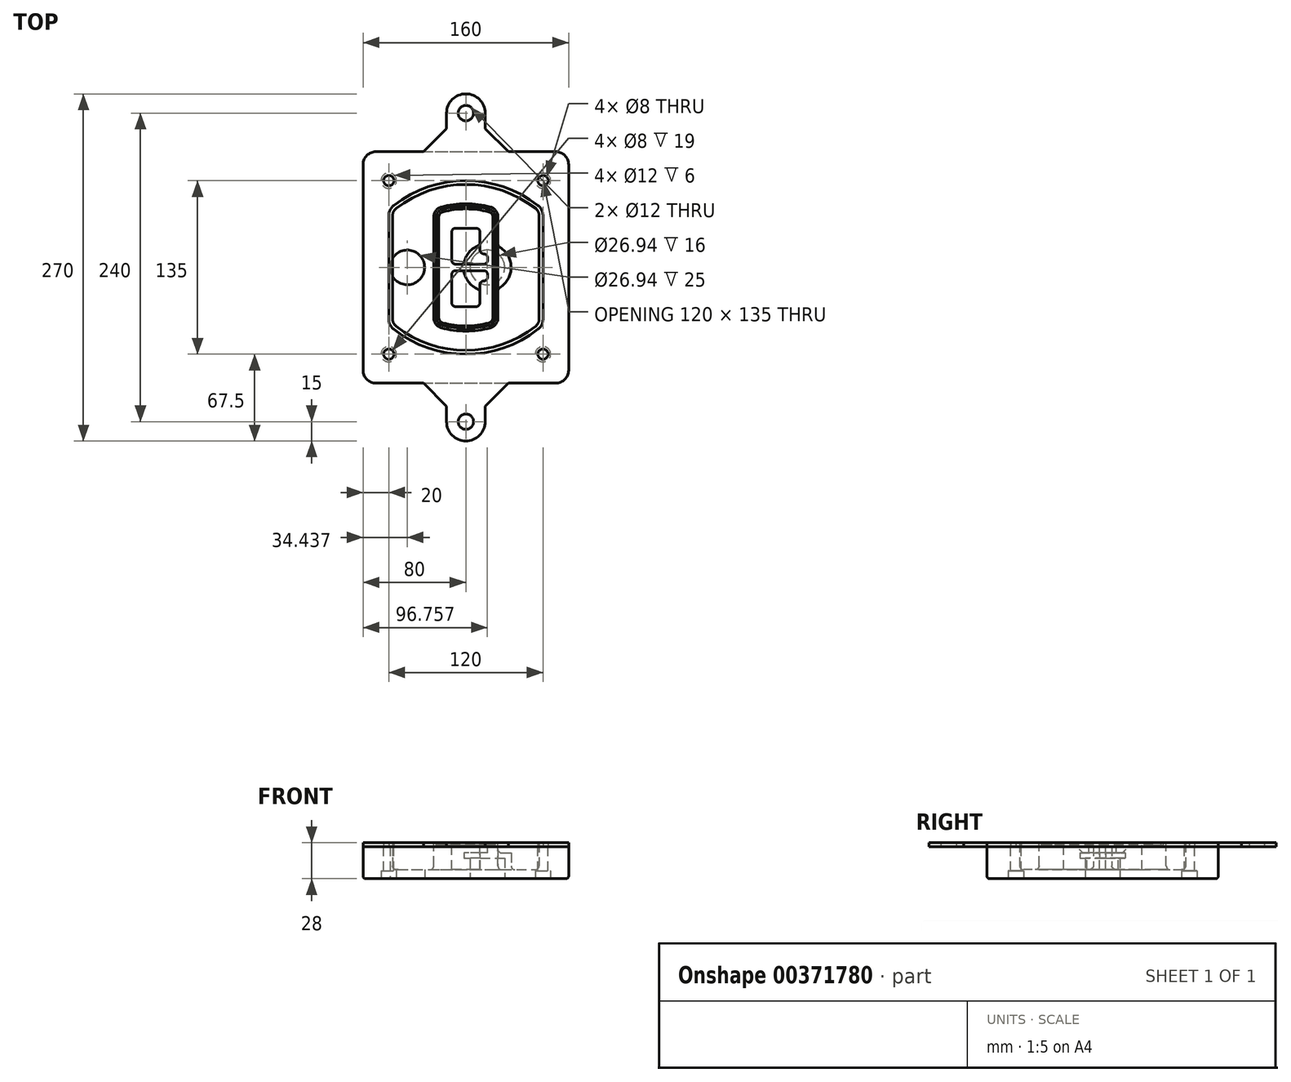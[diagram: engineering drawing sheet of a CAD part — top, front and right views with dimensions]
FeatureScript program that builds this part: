
annotation { "Feature Type Name" : "Feature", "Feature Type Description" : "" }
export const myFeature = defineFeature(function(context is Context, id is Id, definition is map)
    precondition{}
    {
        {
            var Q0;
            Q0=qCreatedBy(makeId("Top.planeOp"),FACE);
            var sketch = newSketch(context, id + "F0", { "sketchPlane" : qUnion([Q0])});
            skPoint(sketch, "E0.rect.middle", {"position": v(0, 0) * mm});
            skLineSegment(sketch, "E1.bottom", {"start": v(-70, -90) * mm, "end": v(70, -90) * mm});
            skLineSegment(sketch, "E1.top", {"start": v(-70, 90) * mm, "end": v(70, 90) * mm});
            skLineSegment(sketch, "E1.left", {"start": v(-80, -80) * mm, "end": v(-80, 80) * mm});
            skLineSegment(sketch, "E1.right", {"start": v(80, -80) * mm, "end": v(80, 80) * mm});
            skLineSegment(sketch, "E2", {"start": v(-80, 90) * mm, "end": v(80, -90) * mm, "construction": true});
            skLineSegment(sketch, "E3", {"start": v(80, 90) * mm, "end": v(-80, -90) * mm, "construction": true});
            skCircle(sketch, "E4", {"center": v(-60, 67.5) * mm, "radius": 4 * mm});
            skCircle(sketch, "E5", {"center": v(60, 67.5) * mm, "radius": 4 * mm});
            skCircle(sketch, "E6", {"center": v(60, -67.5) * mm, "radius": 4 * mm});
            skCircle(sketch, "E7", {"center": v(-60, -67.5) * mm, "radius": 4 * mm});
            skLineSegment(sketch, "E8", {"start": v(-60, 67.5) * mm, "end": v(60, 67.5) * mm, "construction": true});
            skLineSegment(sketch, "E9", {"start": v(60, 67.5) * mm, "end": v(60, -67.5) * mm, "construction": true});
            skLineSegment(sketch, "E10", {"start": v(60, -67.5) * mm, "end": v(-60, -67.5) * mm, "construction": true});
            skLineSegment(sketch, "E11", {"start": v(-60, -67.5) * mm, "end": v(-60, 67.5) * mm, "construction": true});
            skLineSegment(sketch, "E12", {"start": v(-60, 40.3) * mm, "end": v(-60, -40.3) * mm});
            skLineSegment(sketch, "E13", {"start": v(60, 40.3) * mm, "end": v(60, -40.3) * mm});
            skArc(sketch, "E14", {"start": v(56.15, 48.18) * mm, "mid": v(0, 67.5) * mm, "end": v(-56.15, 48.18) * mm});
            skArc(sketch, "E15", {"start": v(-56.15, -48.18) * mm, "mid": v(0, -67.5) * mm, "end": v(56.15, -48.18) * mm});
            skLineSegment(sketch, "E16", {"start": v(-60, 0) * mm, "end": v(60, 0) * mm, "construction": true});
            skPoint(sketch, "E17.visualSharp", {"position": v(-60, -45) * mm});
            skArc(sketch, "E17.filletArc", {"start": v(-60, -40.3) * mm, "mid": v(-58.99, -44.68) * mm, "end": v(-56.15, -48.18) * mm});
            skPoint(sketch, "E18.visualSharp", {"position": v(-60, 45) * mm});
            skArc(sketch, "E18.filletArc", {"start": v(-56.15, 48.18) * mm, "mid": v(-58.99, 44.68) * mm, "end": v(-60, 40.3) * mm});
            skPoint(sketch, "E19.visualSharp", {"position": v(60, 45) * mm});
            skArc(sketch, "E19.filletArc", {"start": v(60, 40.3) * mm, "mid": v(58.99, 44.68) * mm, "end": v(56.15, 48.18) * mm});
            skPoint(sketch, "E20.visualSharp", {"position": v(60, -45) * mm});
            skArc(sketch, "E20.filletArc", {"start": v(56.15, -48.18) * mm, "mid": v(58.99, -44.68) * mm, "end": v(60, -40.3) * mm});
            skPoint(sketch, "E21.visualSharp", {"position": v(-80, 90) * mm});
            skArc(sketch, "E21.filletArc", {"start": v(-70, 90) * mm, "mid": v(-77.07, 87.07) * mm, "end": v(-80, 80) * mm});
            skPoint(sketch, "E22.visualSharp", {"position": v(80, 90) * mm});
            skArc(sketch, "E22.filletArc", {"start": v(80, 80) * mm, "mid": v(77.07, 87.07) * mm, "end": v(70, 90) * mm});
            skPoint(sketch, "E23.visualSharp", {"position": v(80, -90) * mm});
            skArc(sketch, "E23.filletArc", {"start": v(70, -90) * mm, "mid": v(77.07, -87.07) * mm, "end": v(80, -80) * mm});
            skPoint(sketch, "E24.visualSharp", {"position": v(-80, -90) * mm});
            skArc(sketch, "E24.filletArc", {"start": v(-80, -80) * mm, "mid": v(-77.07, -87.07) * mm, "end": v(-70, -90) * mm});
            skArc(sketch, "E25.0", {"start": v(57, 40.3) * mm, "mid": v(56.3, 43.36) * mm, "end": v(54.3, 45.81) * mm});
            skLineSegment(sketch, "E25.1", {"start": v(57, 40.3) * mm, "end": v(57, -40.3) * mm});
            skArc(sketch, "E25.2", {"start": v(54.3, -45.81) * mm, "mid": v(56.3, -43.36) * mm, "end": v(57, -40.3) * mm});
            skArc(sketch, "E25.3", {"start": v(-54.3, -45.81) * mm, "mid": v(0, -64.5) * mm, "end": v(54.3, -45.81) * mm});
            skArc(sketch, "E25.4", {"start": v(-57, -40.3) * mm, "mid": v(-56.3, -43.36) * mm, "end": v(-54.3, -45.81) * mm});
            skArc(sketch, "E25.5", {"start": v(54.3, 45.81) * mm, "mid": v(0, 64.5) * mm, "end": v(-54.3, 45.81) * mm});
            skLineSegment(sketch, "E25.6", {"start": v(-57, 40.3) * mm, "end": v(-57, -40.3) * mm});
            skArc(sketch, "E25.7", {"start": v(-54.3, 45.81) * mm, "mid": v(-56.3, 43.36) * mm, "end": v(-57, 40.3) * mm});
            skArc(sketch, "E26.0", {"start": v(-58.62, 51.33) * mm, "mid": v(-62.58, 46.43) * mm, "end": v(-64, 40.3) * mm});
            skArc(sketch, "E26.1", {"start": v(58.62, 51.33) * mm, "mid": v(0, 71.5) * mm, "end": v(-58.62, 51.33) * mm});
            skArc(sketch, "E26.2", {"start": v(64, 40.3) * mm, "mid": v(62.58, 46.43) * mm, "end": v(58.62, 51.33) * mm});
            skLineSegment(sketch, "E26.3", {"start": v(64, 40.3) * mm, "end": v(64, -40.3) * mm});
            skArc(sketch, "E26.4", {"start": v(58.62, -51.33) * mm, "mid": v(62.58, -46.43) * mm, "end": v(64, -40.3) * mm});
            skLineSegment(sketch, "E26.5", {"start": v(-64, 40.3) * mm, "end": v(-64, -40.3) * mm});
            skArc(sketch, "E26.6", {"start": v(-58.62, -51.33) * mm, "mid": v(0, -71.5) * mm, "end": v(58.62, -51.33) * mm});
            skArc(sketch, "E26.7", {"start": v(-64, -40.3) * mm, "mid": v(-62.58, -46.43) * mm, "end": v(-58.62, -51.33) * mm});
            skSolve(sketch);
        }
        {
            var Q0;
            Q0=makeQuery(id+"F0.imprint","IMPRINT",FACE,{"disambiguationData":[TD([[makeQuery(id+"F0.imprint","IMPRINT",EDGE,{"derivedFrom":sQuery(id+"F0.wireOp",EDGE,"E1.bottom")}),1.0]])]});
            var Q1;
            Q1=makeQuery(id+"F0.imprint","IMPRINT",FACE,{"disambiguationData":[TD([[makeQuery(id+"F0.imprint","IMPRINT",EDGE,{"derivedFrom":sQuery(id+"F0.wireOp",EDGE,"E12")}),1.0]])]});
            var Q2;
            Q2=makeQuery(id+"F0.imprint","IMPRINT",FACE,{"disambiguationData":[TD([[makeQuery(id+"F0.imprint","IMPRINT",EDGE,{"derivedFrom":sQuery(id+"F0.wireOp",EDGE,"E25.0")}),1.0]])]});
            var Q3;
            Q3=makeQuery(id+"F0.imprint","IMPRINT",FACE,{"disambiguationData":[TD([[makeQuery(id+"F0.imprint","IMPRINT",EDGE,{"derivedFrom":sQuery(id+"F0.wireOp",EDGE,"E12")}),-1.0]])]});
            extrude(context, id + "F1", {"entities" : qUnion([Q0, Q1, Q2, Q3]), "oppositeDirection" : true, "depth" : 25 * mm});
        }
        {
            var Q0;
            Q0=makeQuery(id+"F0.imprint","IMPRINT",FACE,{"disambiguationData":[TD([[makeQuery(id+"F0.imprint","IMPRINT",EDGE,{"derivedFrom":sQuery(id+"F0.wireOp",EDGE,"E12")}),1.0]])]});
            extrude(context, id + "F2", {"entities" : qUnion([Q0]), "operationType" : NewBodyOperationType.ADD, "depth" : 3 * mm});
        }
        {
            var Q0;
            Q0=makeQuery(id+"F0.imprint","IMPRINT",FACE,{"disambiguationData":[TD([[makeQuery(id+"F0.imprint","IMPRINT",EDGE,{"derivedFrom":sQuery(id+"F0.wireOp",EDGE,"E25.0")}),1.0]])]});
            extrude(context, id + "F3", {"entities" : qUnion([Q0]), "operationType" : NewBodyOperationType.REMOVE, "oppositeDirection" : true, "depth" : 18 * mm});
        }
        {
            var Q0;
            Q0=makeQuery(id+"F2.opExtrude","CAP_FACE",FACE,{"disambiguationData":[OSD([sQuery(id+"F0.wireOp",EDGE,"E12"),sQuery(id+"F0.wireOp",EDGE,"E13"),sQuery(id+"F0.wireOp",EDGE,"E14"),sQuery(id+"F0.wireOp",EDGE,"E15"),sQuery(id+"F0.wireOp",EDGE,"E17.filletArc"),sQuery(id+"F0.wireOp",EDGE,"E18.filletArc"),sQuery(id+"F0.wireOp",EDGE,"E19.filletArc"),sQuery(id+"F0.wireOp",EDGE,"E20.filletArc"),sQuery(id+"F0.wireOp",EDGE,"E25.0"),sQuery(id+"F0.wireOp",EDGE,"E25.1"),sQuery(id+"F0.wireOp",EDGE,"E25.2"),sQuery(id+"F0.wireOp",EDGE,"E25.3"),sQuery(id+"F0.wireOp",EDGE,"E25.4"),sQuery(id+"F0.wireOp",EDGE,"E25.5"),sQuery(id+"F0.wireOp",EDGE,"E25.6"),sQuery(id+"F0.wireOp",EDGE,"E25.7")])],"isStart":false});
            var sketch = newSketch(context, id + "F4", { "sketchPlane" : qUnion([Q0])});
            skArc(sketch, "E27.0", {"start": v(-19.08, -46.97) * mm, "mid": v(0, -49.5) * mm, "end": v(19.08, -46.97) * mm});
            skArc(sketch, "E28.0", {"start": v(19.08, 46.97) * mm, "mid": v(0, 49.5) * mm, "end": v(-19.08, 46.97) * mm});
            skLineSegment(sketch, "E29", {"start": v(-25, 39.25) * mm, "end": v(-25, -39.25) * mm});
            skLineSegment(sketch, "E30", {"start": v(25, 39.25) * mm, "end": v(25, -39.25) * mm});
            skLineSegment(sketch, "E31", {"start": v(-25, 45.1) * mm, "end": v(25, 45.1) * mm, "construction": true});
            skLineSegment(sketch, "E32", {"start": v(-25, -45.1) * mm, "end": v(25, -45.1) * mm, "construction": true});
            skPoint(sketch, "E33.visualSharp", {"position": v(-25, 45.1) * mm});
            skArc(sketch, "E33.filletArc", {"start": v(-19.08, 46.97) * mm, "mid": v(-23.35, 44.11) * mm, "end": v(-25, 39.25) * mm});
            skPoint(sketch, "E34.visualSharp", {"position": v(25, 45.1) * mm});
            skArc(sketch, "E34.filletArc", {"start": v(25, 39.25) * mm, "mid": v(23.35, 44.11) * mm, "end": v(19.08, 46.97) * mm});
            skPoint(sketch, "E35.visualSharp", {"position": v(25, -45.1) * mm});
            skArc(sketch, "E35.filletArc", {"start": v(19.08, -46.97) * mm, "mid": v(23.35, -44.11) * mm, "end": v(25, -39.25) * mm});
            skPoint(sketch, "E36.visualSharp", {"position": v(-25, -45.1) * mm});
            skArc(sketch, "E36.filletArc", {"start": v(-25, -39.25) * mm, "mid": v(-23.35, -44.11) * mm, "end": v(-19.08, -46.97) * mm});
            skArc(sketch, "E37.0", {"start": v(54.3, 45.81) * mm, "mid": v(0, 64.5) * mm, "end": v(-54.3, 45.81) * mm});
            skArc(sketch, "E37.1", {"start": v(-54.3, 45.81) * mm, "mid": v(-56.3, 43.36) * mm, "end": v(-57, 40.3) * mm});
            skLineSegment(sketch, "E37.2", {"start": v(-57, 40.3) * mm, "end": v(-57, -40.3) * mm});
            skArc(sketch, "E37.3", {"start": v(-57, -40.3) * mm, "mid": v(-56.3, -43.36) * mm, "end": v(-54.3, -45.81) * mm});
            skArc(sketch, "E37.4", {"start": v(-54.3, -45.81) * mm, "mid": v(0, -64.5) * mm, "end": v(54.3, -45.81) * mm});
            skArc(sketch, "E37.5", {"start": v(54.3, -45.81) * mm, "mid": v(56.3, -43.36) * mm, "end": v(57, -40.3) * mm});
            skLineSegment(sketch, "E37.6", {"start": v(57, 40.3) * mm, "end": v(57, -40.3) * mm});
            skArc(sketch, "E37.7", {"start": v(57, 40.3) * mm, "mid": v(56.3, 43.36) * mm, "end": v(54.3, 45.81) * mm});
            skLineSegment(sketch, "E38.0", {"start": v(23, 39.25) * mm, "end": v(23, -39.25) * mm});
            skArc(sketch, "E38.1", {"start": v(18.56, -45.04) * mm, "mid": v(21.76, -42.9) * mm, "end": v(23, -39.25) * mm});
            skArc(sketch, "E38.2", {"start": v(-18.56, -45.04) * mm, "mid": v(0, -47.5) * mm, "end": v(18.56, -45.04) * mm});
            skArc(sketch, "E38.3", {"start": v(-23, -39.25) * mm, "mid": v(-21.76, -42.9) * mm, "end": v(-18.56, -45.04) * mm});
            skLineSegment(sketch, "E38.4", {"start": v(-23, 39.25) * mm, "end": v(-23, -39.25) * mm});
            skArc(sketch, "E38.5", {"start": v(23, 39.25) * mm, "mid": v(21.76, 42.9) * mm, "end": v(18.56, 45.04) * mm});
            skArc(sketch, "E38.6", {"start": v(-18.56, 45.04) * mm, "mid": v(-21.76, 42.9) * mm, "end": v(-23, 39.25) * mm});
            skArc(sketch, "E38.7", {"start": v(18.56, 45.04) * mm, "mid": v(0, 47.5) * mm, "end": v(-18.56, 45.04) * mm});
            skArc(sketch, "E39.0", {"start": v(21, 39.25) * mm, "mid": v(20.18, 41.68) * mm, "end": v(18.04, 43.1) * mm});
            skLineSegment(sketch, "E39.1", {"start": v(21, 39.25) * mm, "end": v(21, -39.25) * mm});
            skArc(sketch, "E39.2", {"start": v(18.04, -43.1) * mm, "mid": v(20.18, -41.68) * mm, "end": v(21, -39.25) * mm});
            skArc(sketch, "E39.3", {"start": v(-18.04, -43.1) * mm, "mid": v(0, -45.5) * mm, "end": v(18.04, -43.1) * mm});
            skArc(sketch, "E39.4", {"start": v(-21, -39.25) * mm, "mid": v(-20.18, -41.68) * mm, "end": v(-18.04, -43.1) * mm});
            skArc(sketch, "E39.5", {"start": v(18.04, 43.1) * mm, "mid": v(0, 45.5) * mm, "end": v(-18.04, 43.1) * mm});
            skLineSegment(sketch, "E39.6", {"start": v(-21, 39.25) * mm, "end": v(-21, -39.25) * mm});
            skArc(sketch, "E39.7", {"start": v(-18.04, 43.1) * mm, "mid": v(-20.18, 41.68) * mm, "end": v(-21, 39.25) * mm});
            skLineSegment(sketch, "E40", {"start": v(-25, 0) * mm, "end": v(25, 0) * mm, "construction": true});
            skLineSegment(sketch, "E41", {"start": v(-11, 5.5) * mm, "end": v(-11, 27.5) * mm});
            skLineSegment(sketch, "E42", {"start": v(-8, 30.5) * mm, "end": v(8, 30.5) * mm});
            skLineSegment(sketch, "E43", {"start": v(11, 27.5) * mm, "end": v(11, 13.5) * mm});
            skLineSegment(sketch, "E44", {"start": v(14, 10.5) * mm, "end": v(14, 10.5) * mm});
            skLineSegment(sketch, "E45", {"start": v(17, 7.5) * mm, "end": v(17, 5.5) * mm});
            skLineSegment(sketch, "E46", {"start": v(14, 2.5) * mm, "end": v(-8, 2.5) * mm});
            skPoint(sketch, "E47.visualSharp", {"position": v(-11, 30.5) * mm});
            skArc(sketch, "E47.filletArc", {"start": v(-8, 30.5) * mm, "mid": v(-10.12, 29.62) * mm, "end": v(-11, 27.5) * mm});
            skPoint(sketch, "E48.visualSharp", {"position": v(11, 30.5) * mm});
            skArc(sketch, "E48.filletArc", {"start": v(11, 27.5) * mm, "mid": v(10.12, 29.62) * mm, "end": v(8, 30.5) * mm});
            skPoint(sketch, "E49.visualSharp", {"position": v(11, 10.5) * mm});
            skArc(sketch, "E49.filletArc", {"start": v(11, 13.5) * mm, "mid": v(11.88, 11.38) * mm, "end": v(14, 10.5) * mm});
            skPoint(sketch, "E50.visualSharp", {"position": v(17, 10.5) * mm});
            skArc(sketch, "E50.filletArc", {"start": v(17, 7.5) * mm, "mid": v(16.12, 9.62) * mm, "end": v(14, 10.5) * mm});
            skPoint(sketch, "E51.visualSharp", {"position": v(17, 2.5) * mm});
            skArc(sketch, "E51.filletArc", {"start": v(14, 2.5) * mm, "mid": v(16.12, 3.38) * mm, "end": v(17, 5.5) * mm});
            skPoint(sketch, "E52.visualSharp", {"position": v(-11, 2.5) * mm});
            skArc(sketch, "E52.filletArc", {"start": v(-11, 5.5) * mm, "mid": v(-10.12, 3.38) * mm, "end": v(-8, 2.5) * mm});
            skLineSegment(sketch, "E53.0.MirrorCS", {"start": v(14, -2.5) * mm, "end": v(-8, -2.5) * mm});
            skArc(sketch, "E54.0.MirrorCS", {"start": v(-11, -5.5) * mm, "mid": v(-10.12, -3.38) * mm, "end": v(-8, -2.5) * mm});
            skLineSegment(sketch, "E55.0.MirrorCS", {"start": v(-11, -5.5) * mm, "end": v(-11, -27.5) * mm});
            skArc(sketch, "E56.0.MirrorCS", {"start": v(-8, -30.5) * mm, "mid": v(-10.12, -29.62) * mm, "end": v(-11, -27.5) * mm});
            skLineSegment(sketch, "E57.0.MirrorCS", {"start": v(-8, -30.5) * mm, "end": v(8, -30.5) * mm});
            skArc(sketch, "E58.0.MirrorCS", {"start": v(11, -27.5) * mm, "mid": v(10.12, -29.62) * mm, "end": v(8, -30.5) * mm});
            skLineSegment(sketch, "E59.0.MirrorCS", {"start": v(11, -27.5) * mm, "end": v(11, -13.5) * mm});
            skArc(sketch, "E60.0.MirrorCS", {"start": v(11, -13.5) * mm, "mid": v(11.88, -11.38) * mm, "end": v(14, -10.5) * mm});
            skArc(sketch, "E61.0.MirrorCS", {"start": v(17, -7.5) * mm, "mid": v(16.12, -9.62) * mm, "end": v(14, -10.5) * mm});
            skLineSegment(sketch, "E62.0.MirrorCS", {"start": v(17, -7.5) * mm, "end": v(17, -5.5) * mm});
            skArc(sketch, "E63.0.MirrorCS", {"start": v(14, -2.5) * mm, "mid": v(16.12, -3.38) * mm, "end": v(17, -5.5) * mm});
            skSolve(sketch);
        }
        {
            var Q0;
            Q0=makeQuery(id+"F4.imprint","IMPRINT",FACE,{"disambiguationData":[TD([[makeQuery(id+"F4.imprint","IMPRINT",EDGE,{"derivedFrom":sQuery(id+"F4.wireOp",EDGE,"E27.0")}),1.0]])]});
            var Q1;
            Q1=makeQuery(id+"F4.imprint","IMPRINT",FACE,{"disambiguationData":[TD([[makeQuery(id+"F4.imprint","IMPRINT",EDGE,{"derivedFrom":sQuery(id+"F4.wireOp",EDGE,"E38.0")}),-1.0]])]});
            var Q2;
            Q2=makeQuery(id+"F4.imprint","IMPRINT",FACE,{"disambiguationData":[TD([[makeQuery(id+"F4.imprint","IMPRINT",EDGE,{"derivedFrom":sQuery(id+"F4.wireOp",EDGE,"E39.0")}),1.0]])]});
            extrude(context, id + "F5", {"entities" : qUnion([Q0, Q1, Q2]), "operationType" : NewBodyOperationType.ADD, "endBound" : BoundingType.UP_TO_NEXT, "oppositeDirection" : true, "depth" : 25 * mm});
        }
        {
            var Q0;
            Q0=makeQuery(id+"F4.imprint","IMPRINT",FACE,{"disambiguationData":[TD([[makeQuery(id+"F4.imprint","IMPRINT",EDGE,{"derivedFrom":sQuery(id+"F4.wireOp",EDGE,"E38.0")}),-1.0]])]});
            extrude(context, id + "F6", {"entities" : qUnion([Q0]), "operationType" : NewBodyOperationType.REMOVE, "oppositeDirection" : true, "depth" : 2 * mm});
        }
        {
            var Q0;
            Q0=makeQuery(id+"F1.opExtrude","CAP_FACE",FACE,{"disambiguationData":[OSD([sQuery(id+"F0.wireOp",EDGE,"E1.bottom"),sQuery(id+"F0.wireOp",EDGE,"E1.top"),sQuery(id+"F0.wireOp",EDGE,"E1.left"),sQuery(id+"F0.wireOp",EDGE,"E1.right"),sQuery(id+"F0.wireOp",EDGE,"E4"),sQuery(id+"F0.wireOp",EDGE,"E5"),sQuery(id+"F0.wireOp",EDGE,"E6"),sQuery(id+"F0.wireOp",EDGE,"E7"),sQuery(id+"F0.wireOp",EDGE,"E21.filletArc"),sQuery(id+"F0.wireOp",EDGE,"E22.filletArc"),sQuery(id+"F0.wireOp",EDGE,"E23.filletArc"),sQuery(id+"F0.wireOp",EDGE,"E24.filletArc")])],"isStart":false});
            var sketch = newSketch(context, id + "F7", { "sketchPlane" : qUnion([Q0])});
            skCircle(sketch, "E64", {"center": v(16.76, 0) * mm, "radius": 13.47 * mm});
            skCircle(sketch, "E65", {"center": v(-45.56, 0) * mm, "radius": 13.47 * mm});
            skLineSegment(sketch, "E66", {"start": v(80, 0) * mm, "end": v(-80, 0) * mm});
            skCircle(sketch, "E67", {"center": v(16.76, 0) * mm, "radius": 18.47 * mm});
            skCircle(sketch, "E68", {"center": v(60, -67.5) * mm, "radius": 6 * mm});
            skCircle(sketch, "E69", {"center": v(-60, -67.5) * mm, "radius": 6 * mm});
            skCircle(sketch, "E70", {"center": v(-60, 67.5) * mm, "radius": 6 * mm});
            skCircle(sketch, "E71", {"center": v(60, 67.5) * mm, "radius": 6 * mm});
            skSolve(sketch);
        }
        {
            var Q0;
            {var subQ1=sQuery(id+"F7.wireOp",EDGE,"E66");var subQ4=sQuery(id+"F7.wireOp",EDGE,"E64");var subQ6=makeQuery(id+"F7.imprint","INTERSECT",VERTEX,{"disambiguationData":[OD(0.0)],"derivedFrom":[subQ4,subQ1]});Q0=makeQuery(id+"F7.imprint","IMPRINT",FACE,{"disambiguationData":[TD([[makeQuery(id+"F7.imprint","IMPRINT",EDGE,{"disambiguationData":[TD([[subQ6,-1.0]])],"derivedFrom":subQ4}),-1.0]])]});}
            var Q1;
            {var subQ0=sQuery(id+"F7.wireOp",EDGE,"E66");var subQ1=sQuery(id+"F7.wireOp",EDGE,"E64");var subQ3=makeQuery(id+"F7.imprint","INTERSECT",VERTEX,{"disambiguationData":[OD(0.0)],"derivedFrom":[subQ1,subQ0]});Q1=makeQuery(id+"F7.imprint","IMPRINT",FACE,{"disambiguationData":[TD([[makeQuery(id+"F7.imprint","IMPRINT",EDGE,{"disambiguationData":[TD([[subQ3,-1.0]])],"derivedFrom":subQ1}),1.0]])]});}
            var Q2;
            {var subQ0=sQuery(id+"F7.wireOp",EDGE,"E66");var subQ1=sQuery(id+"F7.wireOp",EDGE,"E64");var subQ3=makeQuery(id+"F7.imprint","INTERSECT",VERTEX,{"disambiguationData":[OD(0.0)],"derivedFrom":[subQ1,subQ0]});Q2=makeQuery(id+"F7.imprint","IMPRINT",FACE,{"disambiguationData":[TD([[makeQuery(id+"F7.imprint","IMPRINT",EDGE,{"disambiguationData":[TD([[subQ3,1.0]])],"derivedFrom":subQ1}),1.0]])]});}
            var Q3;
            {var subQ1=sQuery(id+"F7.wireOp",EDGE,"E66");var subQ4=sQuery(id+"F7.wireOp",EDGE,"E64");var subQ6=makeQuery(id+"F7.imprint","INTERSECT",VERTEX,{"disambiguationData":[OD(0.0)],"derivedFrom":[subQ4,subQ1]});Q3=makeQuery(id+"F7.imprint","IMPRINT",FACE,{"disambiguationData":[TD([[makeQuery(id+"F7.imprint","IMPRINT",EDGE,{"disambiguationData":[TD([[subQ6,1.0]])],"derivedFrom":subQ4}),-1.0]])]});}
            extrude(context, id + "F8", {"entities" : qUnion([Q0, Q1, Q2, Q3]), "operationType" : NewBodyOperationType.ADD, "oppositeDirection" : true, "depth" : 20 * mm});
        }
        {
            var Q0;
            {var subQ0=sQuery(id+"F7.wireOp",EDGE,"E66");var subQ1=sQuery(id+"F7.wireOp",EDGE,"E64");var subQ3=makeQuery(id+"F7.imprint","INTERSECT",VERTEX,{"disambiguationData":[OD(0.0)],"derivedFrom":[subQ1,subQ0]});Q0=makeQuery(id+"F7.imprint","IMPRINT",FACE,{"disambiguationData":[TD([[makeQuery(id+"F7.imprint","IMPRINT",EDGE,{"disambiguationData":[TD([[subQ3,-1.0]])],"derivedFrom":subQ1}),1.0]])]});}
            var Q1;
            {var subQ0=sQuery(id+"F7.wireOp",EDGE,"E66");var subQ1=sQuery(id+"F7.wireOp",EDGE,"E64");var subQ3=makeQuery(id+"F7.imprint","INTERSECT",VERTEX,{"disambiguationData":[OD(0.0)],"derivedFrom":[subQ1,subQ0]});Q1=makeQuery(id+"F7.imprint","IMPRINT",FACE,{"disambiguationData":[TD([[makeQuery(id+"F7.imprint","IMPRINT",EDGE,{"disambiguationData":[TD([[subQ3,1.0]])],"derivedFrom":subQ1}),1.0]])]});}
            extrude(context, id + "F9", {"entities" : qUnion([Q0, Q1]), "operationType" : NewBodyOperationType.REMOVE, "oppositeDirection" : true, "depth" : 16 * mm});
        }
        {
            var Q0;
            {var subQ0=sQuery(id+"F7.wireOp",EDGE,"E66");var subQ1=sQuery(id+"F7.wireOp",EDGE,"E65");var subQ3=makeQuery(id+"F7.imprint","INTERSECT",VERTEX,{"disambiguationData":[OD(0.0)],"derivedFrom":[subQ1,subQ0]});Q0=makeQuery(id+"F7.imprint","IMPRINT",FACE,{"disambiguationData":[TD([[makeQuery(id+"F7.imprint","IMPRINT",EDGE,{"disambiguationData":[TD([[subQ3,-1.0]])],"derivedFrom":subQ1}),1.0]])]});}
            var Q1;
            {var subQ0=sQuery(id+"F7.wireOp",EDGE,"E66");var subQ1=sQuery(id+"F7.wireOp",EDGE,"E65");var subQ3=makeQuery(id+"F7.imprint","INTERSECT",VERTEX,{"disambiguationData":[OD(0.0)],"derivedFrom":[subQ1,subQ0]});Q1=makeQuery(id+"F7.imprint","IMPRINT",FACE,{"disambiguationData":[TD([[makeQuery(id+"F7.imprint","IMPRINT",EDGE,{"disambiguationData":[TD([[subQ3,1.0]])],"derivedFrom":subQ1}),1.0]])]});}
            extrude(context, id + "F10", {"entities" : qUnion([Q0, Q1]), "operationType" : NewBodyOperationType.REMOVE, "oppositeDirection" : true, "depth" : 25 * mm});
        }
        {
            var Q0;
            Q0=makeQuery(id+"F7.imprint","IMPRINT",FACE,{"disambiguationData":[TD([[makeQuery(id+"F7.imprint","IMPRINT",EDGE,{"derivedFrom":sQuery(id+"F7.wireOp",EDGE,"E68")}),1.0]])]});
            var Q1;
            Q1=makeQuery(id+"F7.imprint","IMPRINT",FACE,{"disambiguationData":[TD([[makeQuery(id+"F7.imprint","IMPRINT",EDGE,{"derivedFrom":makeQuery(id+"F1.opExtrude","CAP_EDGE",EDGE,{"disambiguationData":[OSD([sQuery(id+"F0.wireOp",EDGE,"E5")])],"isStart":false})}),-1.0]])]});
            var Q2;
            Q2=makeQuery(id+"F7.imprint","IMPRINT",FACE,{"disambiguationData":[TD([[makeQuery(id+"F7.imprint","IMPRINT",EDGE,{"derivedFrom":sQuery(id+"F7.wireOp",EDGE,"E69")}),1.0]])]});
            var Q3;
            Q3=makeQuery(id+"F7.imprint","IMPRINT",FACE,{"disambiguationData":[TD([[makeQuery(id+"F7.imprint","IMPRINT",EDGE,{"derivedFrom":makeQuery(id+"F1.opExtrude","CAP_EDGE",EDGE,{"disambiguationData":[OSD([sQuery(id+"F0.wireOp",EDGE,"E4")])],"isStart":false})}),-1.0]])]});
            var Q4;
            Q4=makeQuery(id+"F7.imprint","IMPRINT",FACE,{"disambiguationData":[TD([[makeQuery(id+"F7.imprint","IMPRINT",EDGE,{"derivedFrom":sQuery(id+"F7.wireOp",EDGE,"E70")}),1.0]])]});
            var Q5;
            Q5=makeQuery(id+"F7.imprint","IMPRINT",FACE,{"disambiguationData":[TD([[makeQuery(id+"F7.imprint","IMPRINT",EDGE,{"derivedFrom":makeQuery(id+"F1.opExtrude","CAP_EDGE",EDGE,{"disambiguationData":[OSD([sQuery(id+"F0.wireOp",EDGE,"E7")])],"isStart":false})}),-1.0]])]});
            var Q6;
            Q6=makeQuery(id+"F7.imprint","IMPRINT",FACE,{"disambiguationData":[TD([[makeQuery(id+"F7.imprint","IMPRINT",EDGE,{"derivedFrom":sQuery(id+"F7.wireOp",EDGE,"E71")}),1.0]])]});
            var Q7;
            Q7=makeQuery(id+"F7.imprint","IMPRINT",FACE,{"disambiguationData":[TD([[makeQuery(id+"F7.imprint","IMPRINT",EDGE,{"derivedFrom":makeQuery(id+"F1.opExtrude","CAP_EDGE",EDGE,{"disambiguationData":[OSD([sQuery(id+"F0.wireOp",EDGE,"E6")])],"isStart":false})}),-1.0]])]});
            extrude(context, id + "F11", {"entities" : qUnion([Q0, Q1, Q2, Q3, Q4, Q5, Q6, Q7]), "operationType" : NewBodyOperationType.REMOVE, "oppositeDirection" : true, "depth" : 6 * mm});
        }
        {
            var Q0;
            Q0=makeQuery(id+"F9.boolean.opBoolean","COPY",FACE,{"derivedFrom":makeQuery(id+"F9.opExtrude","CAP_FACE",FACE,{"disambiguationData":[OSD([sQuery(id+"F7.wireOp",EDGE,"E64")])],"isStart":false})});
            var sketch = newSketch(context, id + "F12", { "sketchPlane" : qUnion([Q0])});
            skArc(sketch, "E72.0", {"start": v(11, 17.55) * mm, "mid": v(2.57, 11.82) * mm, "end": v(-1.54, 2.5) * mm});
            skArc(sketch, "E72.1", {"start": v(-1.54, -2.5) * mm, "mid": v(2.57, -11.82) * mm, "end": v(11, -17.55) * mm});
            skLineSegment(sketch, "E73", {"start": v(-1.54, -2.5) * mm, "end": v(14, -2.5) * mm});
            skLineSegment(sketch, "E74.0", {"start": v(14, 2.5) * mm, "end": v(-1.54, 2.5) * mm});
            skArc(sketch, "E74.1", {"start": v(14, 2.5) * mm, "mid": v(16.12, 3.38) * mm, "end": v(17, 5.5) * mm});
            skLineSegment(sketch, "E74.2", {"start": v(17, 7.5) * mm, "end": v(17, 5.5) * mm});
            skArc(sketch, "E74.3", {"start": v(17, 7.5) * mm, "mid": v(16.12, 9.62) * mm, "end": v(14, 10.5) * mm});
            skArc(sketch, "E74.4", {"start": v(11, 13.5) * mm, "mid": v(11.88, 11.38) * mm, "end": v(14, 10.5) * mm});
            skLineSegment(sketch, "E74.5", {"start": v(11, 17.55) * mm, "end": v(11, 13.5) * mm});
            skLineSegment(sketch, "E74.7", {"start": v(14, -2.5) * mm, "end": v(-1.54, -2.5) * mm});
            skArc(sketch, "E74.8", {"start": v(14, -2.5) * mm, "mid": v(16.12, -3.38) * mm, "end": v(17, -5.5) * mm});
            skLineSegment(sketch, "E74.9", {"start": v(17, -7.5) * mm, "end": v(17, -5.5) * mm});
            skArc(sketch, "E74.10", {"start": v(17, -7.5) * mm, "mid": v(16.12, -9.62) * mm, "end": v(14, -10.5) * mm});
            skArc(sketch, "E74.11", {"start": v(11, -13.5) * mm, "mid": v(11.88, -11.38) * mm, "end": v(14, -10.5) * mm});
            skLineSegment(sketch, "E74.12", {"start": v(11, -17.55) * mm, "end": v(11, -13.5) * mm});
            skPoint(sketch, "E75.orphan", {"position": v(11, -27.5) * mm});
            skPoint(sketch, "E76.orphan", {"position": v(-8, -2.5) * mm});
            skPoint(sketch, "E77.orphan", {"position": v(-8, 2.5) * mm});
            skPoint(sketch, "E78.orphan", {"position": v(11, 27.5) * mm});
            skSolve(sketch);
        }
        {
            var Q0;
            {var subQ7=sQuery(id+"F12.wireOp",EDGE,"E72.0");var subQ14=sQuery(id+"F12.wireOp",EDGE,"E72.1");var subQ16=sQuery(id+"F12.wireOp",EDGE,"E74.1");var subQ18=sQuery(id+"F12.wireOp",EDGE,"E74.8");Q0=qUnion([makeQuery(id+"F12.imprint","IMPRINT",FACE,{"disambiguationData":[TD([[makeQuery(id+"F12.imprint","IMPRINT",EDGE,{"derivedFrom":subQ7}),1.0]])]}),makeQuery(id+"F12.imprint","IMPRINT",FACE,{"disambiguationData":[TD([[makeQuery(id+"F12.imprint","IMPRINT",EDGE,{"derivedFrom":subQ14}),1.0]])]}),makeQuery(id+"F12.imprint","IMPRINT",FACE,{"disambiguationData":[TD([[makeQuery(id+"F12.imprint","IMPRINT",EDGE,{"derivedFrom":subQ16}),1.0]])]}),makeQuery(id+"F12.imprint","IMPRINT",FACE,{"disambiguationData":[TD([[makeQuery(id+"F12.imprint","IMPRINT",EDGE,{"derivedFrom":subQ18}),-1.0]])]})]);}
            var Q1;
            Q1=makeQuery(id+"F5.boolean.opBoolean","SPLIT",FACE,{"disambiguationData":[TD([makeQuery(id+"F5.opExtrude","SWEPT_FACE",FACE,{"disambiguationData":[OSD([sQuery(id+"F4.wireOp",EDGE,"E41")])]})])],"derivedFrom":makeQuery(id+"F3.boolean.opBoolean","COPY",FACE,{"derivedFrom":makeQuery(id+"F3.opExtrude","CAP_FACE",FACE,{"disambiguationData":[OSD([sQuery(id+"F0.wireOp",EDGE,"E25.0"),sQuery(id+"F0.wireOp",EDGE,"E25.1"),sQuery(id+"F0.wireOp",EDGE,"E25.2"),sQuery(id+"F0.wireOp",EDGE,"E25.3"),sQuery(id+"F0.wireOp",EDGE,"E25.4"),sQuery(id+"F0.wireOp",EDGE,"E25.5"),sQuery(id+"F0.wireOp",EDGE,"E25.6"),sQuery(id+"F0.wireOp",EDGE,"E25.7")])],"isStart":false})})});
            extrude(context, id + "F13", {"entities" : qUnion([Q0]), "operationType" : NewBodyOperationType.REMOVE, "endBound" : BoundingType.UP_TO_SURFACE, "endBoundEntityFace" : qUnion([Q1]), "depth" : 25 * mm});
        }
        {
            var Q0;
            Q0=makeQuery(id+"F3.boolean.opBoolean","COPY",EDGE,{"derivedFrom":makeQuery(id+"F3.opExtrude","CAP_EDGE",EDGE,{"disambiguationData":[OSD([sQuery(id+"F0.wireOp",EDGE,"E25.6")])],"isStart":false})});
            var Q1;
            Q1=makeQuery(id+"F8.boolean.opBoolean","INTERSECT",EDGE,{"derivedFrom":[makeQuery(id+"F5.opExtrude","SWEPT_FACE",FACE,{"disambiguationData":[OSD([sQuery(id+"F4.wireOp",EDGE,"E30")])]}),makeQuery(id+"F8.opExtrude","CAP_FACE",FACE,{"disambiguationData":[OSD([sQuery(id+"F7.wireOp",EDGE,"E67")])],"isStart":false})]});
            var Q2;
            Q2=makeQuery(id+"F8.boolean.opBoolean","INTERSECT",EDGE,{"disambiguationData":[OD(1.0)],"derivedFrom":[makeQuery(id+"F5.opExtrude","SWEPT_FACE",FACE,{"disambiguationData":[OSD([sQuery(id+"F4.wireOp",EDGE,"E30")])]}),makeQuery(id+"F8.opExtrude","SWEPT_FACE",FACE,{"disambiguationData":[OSD([sQuery(id+"F7.wireOp",EDGE,"E67")])]})]});
            var Q3;
            {var subQ0=sQuery(id+"F4.wireOp",EDGE,"E30");Q3=makeQuery(id+"F8.boolean.opBoolean","SPLIT",EDGE,{"disambiguationData":[TD([makeQuery(id+"F5.opExtrude","SWEPT_FACE",FACE,{"disambiguationData":[OSD([sQuery(id+"F4.wireOp",EDGE,"E35.filletArc")])]})])],"derivedFrom":makeQuery(id+"F5.opExtrude","CAP_EDGE",EDGE,{"disambiguationData":[OSD([subQ0])],"isStart":false})});}
            var Q4;
            {var subQ0=sQuery(id+"F0.wireOp",EDGE,"E25.7");var subQ1=sQuery(id+"F0.wireOp",EDGE,"E25.1");var subQ2=sQuery(id+"F0.wireOp",EDGE,"E25.6");var subQ3=sQuery(id+"F0.wireOp",EDGE,"E25.5");var subQ4=sQuery(id+"F0.wireOp",EDGE,"E25.4");var subQ5=sQuery(id+"F0.wireOp",EDGE,"E25.0");var subQ6=sQuery(id+"F0.wireOp",EDGE,"E25.2");var subQ7=sQuery(id+"F0.wireOp",EDGE,"E25.3");Q4=makeQuery(id+"F8.boolean.opBoolean","INTERSECT",EDGE,{"derivedFrom":[makeQuery(id+"F5.boolean.opBoolean","SPLIT",FACE,{"disambiguationData":[TD([makeQuery(id+"F2.opExtrude","SWEPT_FACE",FACE,{"disambiguationData":[OSD([subQ5])]})])],"derivedFrom":makeQuery(id+"F3.boolean.opBoolean","COPY",FACE,{"derivedFrom":makeQuery(id+"F3.opExtrude","CAP_FACE",FACE,{"disambiguationData":[OSD([subQ5,subQ1,subQ6,subQ7,subQ4,subQ3,subQ2,subQ0])],"isStart":false})})}),makeQuery(id+"F8.opExtrude","SWEPT_FACE",FACE,{"disambiguationData":[OSD([sQuery(id+"F7.wireOp",EDGE,"E67")])]})]});}
            var Q5;
            Q5=makeQuery(id+"F8.boolean.opBoolean","INTERSECT",EDGE,{"disambiguationData":[OD(0.0)],"derivedFrom":[makeQuery(id+"F5.opExtrude","SWEPT_FACE",FACE,{"disambiguationData":[OSD([sQuery(id+"F4.wireOp",EDGE,"E30")])]}),makeQuery(id+"F8.opExtrude","SWEPT_FACE",FACE,{"disambiguationData":[OSD([sQuery(id+"F7.wireOp",EDGE,"E67")])]})]});
            fillet(context, id + "F14", {"entities" : qUnion([Q0, Q1, Q2, Q3, Q4, Q5]), "radius" : 3 * mm, "tangentPropagation" : true, "allowEdgeOverflow" : false});
        }
        {
            var Q0;
            Q0=makeQuery(id+"F1.opExtrude","CAP_EDGE",EDGE,{"disambiguationData":[OSD([sQuery(id+"F0.wireOp",EDGE,"E1.bottom")])],"isStart":false});
            fillet(context, id + "F15", {"entities" : qUnion([Q0]), "radius" : 2 * mm, "tangentPropagation" : true, "allowEdgeOverflow" : false});
        }
        {
            var Q0;
            {var subQ0=sQuery(id+"F0.wireOp",EDGE,"E22.filletArc");var subQ1=sQuery(id+"F0.wireOp",EDGE,"E7");var subQ2=sQuery(id+"F0.wireOp",EDGE,"E6");var subQ3=sQuery(id+"F0.wireOp",EDGE,"E5");var subQ4=sQuery(id+"F0.wireOp",EDGE,"E4");var subQ5=sQuery(id+"F0.wireOp",EDGE,"E1.bottom");var subQ6=sQuery(id+"F0.wireOp",EDGE,"E21.filletArc");var subQ7=sQuery(id+"F0.wireOp",EDGE,"E1.top");var subQ8=sQuery(id+"F0.wireOp",EDGE,"E1.left");var subQ9=sQuery(id+"F0.wireOp",EDGE,"E1.right");var subQ10=sQuery(id+"F0.wireOp",EDGE,"E23.filletArc");var subQ11=sQuery(id+"F0.wireOp",EDGE,"E24.filletArc");Q0=makeQuery(id+"F2.boolean.opBoolean","SPLIT",FACE,{"disambiguationData":[TD([makeQuery(id+"F1.opExtrude","SWEPT_FACE",FACE,{"disambiguationData":[OSD([subQ5])]})])],"derivedFrom":makeQuery(id+"F1.opExtrude","CAP_FACE",FACE,{"disambiguationData":[OSD([subQ5,subQ7,subQ8,subQ9,subQ4,subQ3,subQ2,subQ1,subQ6,subQ0,subQ10,subQ11])],"isStart":true})});}
            var sketch = newSketch(context, id + "F16", { "sketchPlane" : qUnion([Q0])});
            skCircle(sketch, "E79", {"center": v(0, 120) * mm, "radius": 6 * mm});
            skLineSegment(sketch, "E80", {"start": v(0, 120) * mm, "end": v(0, 90) * mm, "construction": true});
            skArc(sketch, "E81", {"start": v(-15, 120) * mm, "mid": v(0, 135) * mm, "end": v(15, 120) * mm});
            skLineSegment(sketch, "E82", {"start": v(-15, 120) * mm, "end": v(-15, 108) * mm});
            skLineSegment(sketch, "E83", {"start": v(15, 120) * mm, "end": v(15, 108) * mm});
            skLineSegment(sketch, "E84", {"start": v(15, 108) * mm, "end": v(33, 90) * mm});
            skLineSegment(sketch, "E85", {"start": v(-15, 108) * mm, "end": v(-33, 90) * mm});
            skLineSegment(sketch, "E86", {"start": v(-33, 90) * mm, "end": v(33, 90) * mm, "construction": true});
            skLineSegment(sketch, "E87", {"start": v(-80, 0) * mm, "end": v(80, 0) * mm, "construction": true});
            skLineSegment(sketch, "E88.MirrorCS", {"start": v(-15, -120) * mm, "end": v(-15, -108) * mm});
            skLineSegment(sketch, "E89.MirrorCS", {"start": v(15, -120) * mm, "end": v(15, -108) * mm});
            skLineSegment(sketch, "E90.MirrorCS", {"start": v(-15, -108) * mm, "end": v(-33, -90) * mm});
            skLineSegment(sketch, "E91.MirrorCS", {"start": v(-33, -90) * mm, "end": v(33, -90) * mm, "construction": true});
            skArc(sketch, "E92.MirrorCS", {"start": v(-15, -120) * mm, "mid": v(0, -135) * mm, "end": v(15, -120) * mm});
            skLineSegment(sketch, "E93.MirrorCS", {"start": v(15, -108) * mm, "end": v(33, -90) * mm});
            skCircle(sketch, "E94.MirrorC", {"center": v(0, -120) * mm, "radius": 6 * mm});
            skLineSegment(sketch, "E95.MirrorCS", {"start": v(0, -120) * mm, "end": v(0, -90) * mm, "construction": true});
            skSolve(sketch);
        }
        {
            var Q0;
            Q0=makeQuery(id+"F16.imprint","IMPRINT",FACE,{"disambiguationData":[TD([[makeQuery(id+"F16.imprint","IMPRINT",EDGE,{"derivedFrom":makeQuery(id+"F1.opExtrude","CAP_EDGE",EDGE,{"disambiguationData":[OSD([sQuery(id+"F0.wireOp",EDGE,"E1.left")])],"isStart":true})}),-1.0]])]});
            var Q1;
            Q1=makeQuery(id+"F16.imprint","IMPRINT",FACE,{"disambiguationData":[TD([[makeQuery(id+"F16.imprint","IMPRINT",EDGE,{"derivedFrom":sQuery(id+"F16.wireOp",EDGE,"E79")}),-1.0]])]});
            var Q2;
            Q2=makeQuery(id+"F16.imprint","IMPRINT",FACE,{"disambiguationData":[TD([[makeQuery(id+"F16.imprint","IMPRINT",EDGE,{"derivedFrom":sQuery(id+"F16.wireOp",EDGE,"E88.MirrorCS")}),-1.0]])]});
            var Q3;
            Q3=makeQuery(id+"F2.opExtrude","CAP_FACE",FACE,{"disambiguationData":[OSD([sQuery(id+"F0.wireOp",EDGE,"E12"),sQuery(id+"F0.wireOp",EDGE,"E13"),sQuery(id+"F0.wireOp",EDGE,"E14"),sQuery(id+"F0.wireOp",EDGE,"E15"),sQuery(id+"F0.wireOp",EDGE,"E17.filletArc"),sQuery(id+"F0.wireOp",EDGE,"E18.filletArc"),sQuery(id+"F0.wireOp",EDGE,"E19.filletArc"),sQuery(id+"F0.wireOp",EDGE,"E20.filletArc"),sQuery(id+"F0.wireOp",EDGE,"E25.0"),sQuery(id+"F0.wireOp",EDGE,"E25.1"),sQuery(id+"F0.wireOp",EDGE,"E25.2"),sQuery(id+"F0.wireOp",EDGE,"E25.3"),sQuery(id+"F0.wireOp",EDGE,"E25.4"),sQuery(id+"F0.wireOp",EDGE,"E25.5"),sQuery(id+"F0.wireOp",EDGE,"E25.6"),sQuery(id+"F0.wireOp",EDGE,"E25.7")])],"isStart":false});
            extrude(context, id + "F17", {"entities" : qUnion([Q0, Q1, Q2]), "endBound" : BoundingType.UP_TO_SURFACE, "endBoundEntityFace" : qUnion([Q3]), "depth" : 25 * mm});
        }
    });
